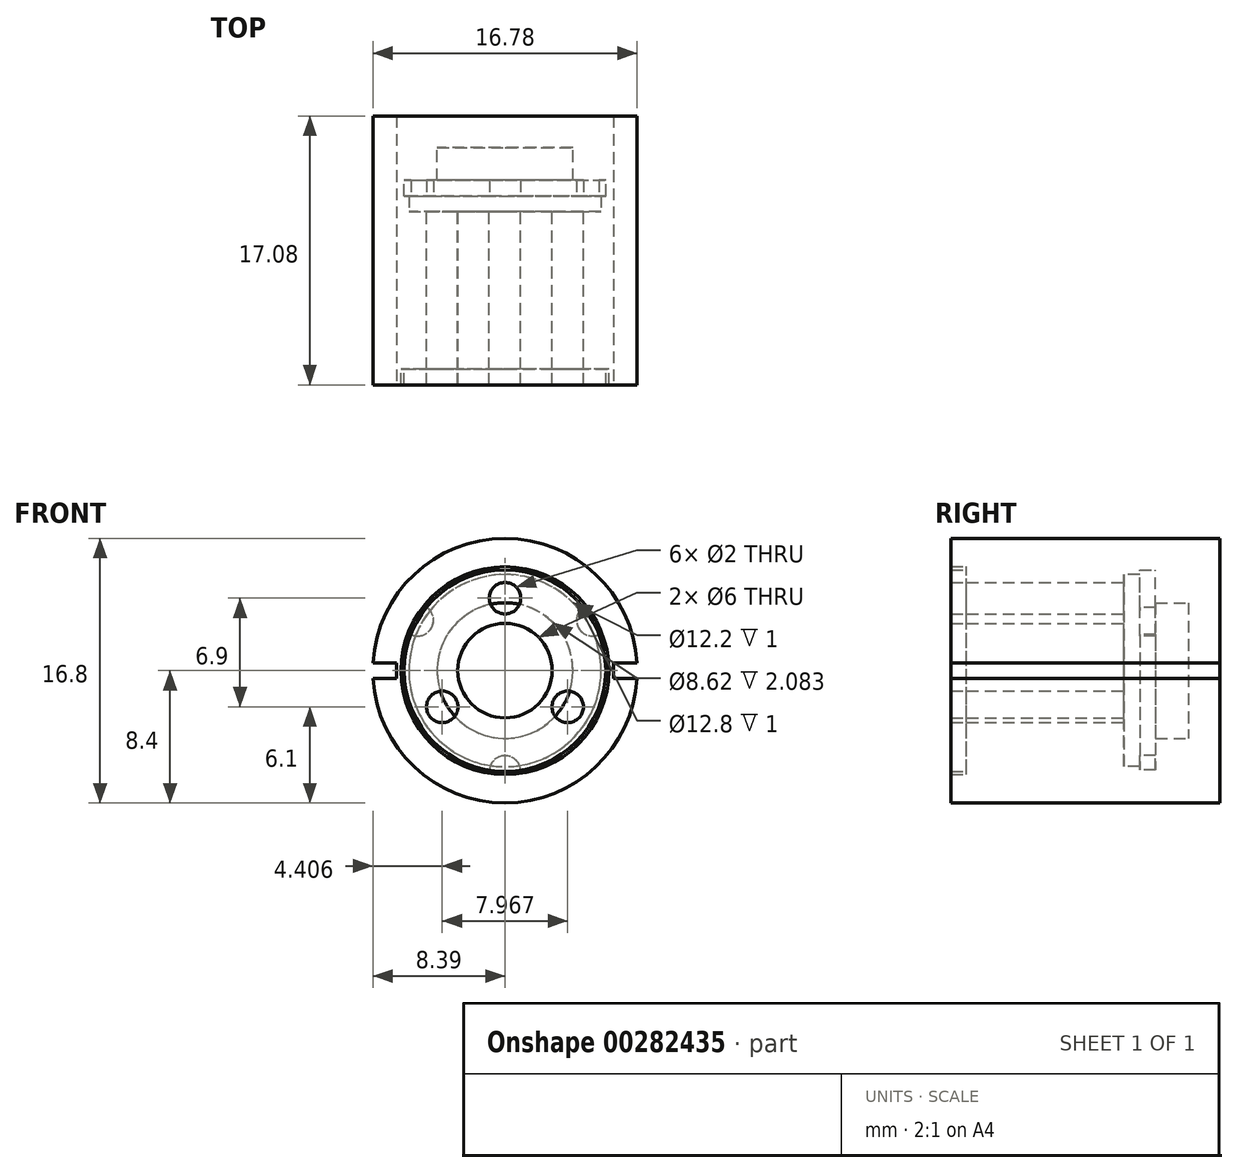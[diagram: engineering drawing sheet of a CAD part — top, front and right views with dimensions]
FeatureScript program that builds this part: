
annotation { "Feature Type Name" : "Feature", "Feature Type Description" : "" }
export const myFeature = defineFeature(function(context is Context, id is Id, definition is map)
    precondition{}
    {
        {
            var Q0;
            Q0=qCreatedBy(makeId("Front.planeOp"),FACE);
            var sketch = newSketch(context, id + "F0", { "sketchPlane" : qUnion([Q0])});
            skCircle(sketch, "E0", {"center": v(0, 0) * mm, "radius": 3 * mm});
            skCircle(sketch, "E1", {"center": v(0, 0) * mm, "radius": 4.6 * mm, "construction": true});
            skCircle(sketch, "E2", {"center": v(0, 0) * mm, "radius": 6.6 * mm});
            skCircle(sketch, "E3", {"center": v(0, 0) * mm, "radius": 10 * mm, "construction": true});
            skCircle(sketch, "E4", {"center": v(0, 4.6) * mm, "radius": 1 * mm});
            skCircle(sketch, "E5.1.0", {"center": v(-3.98, -2.3) * mm, "radius": 1 * mm});
            skCircle(sketch, "E5.2.0", {"center": v(3.98, -2.3) * mm, "radius": 1 * mm});
            skSolve(sketch);
        }
        {
            var Q0;
            Q0 = qSketchRegion(id + "F0", true);
            extrude(context, id + "F1", {"entities" : qUnion([Q0]), "depth" : 10 * mm, "offsetDistance" : 25 * mm});
        }
        {
            var Q0;
            Q0=makeQuery(id+"F1.opExtrude","CAP_FACE",FACE,{"disambiguationData":[OSD([sQuery(id+"F0.wireOp",EDGE,"E0"),sQuery(id+"F0.wireOp",EDGE,"E2"),sQuery(id+"F0.wireOp",EDGE,"E4"),sQuery(id+"F0.wireOp",EDGE,"E5.1.0"),sQuery(id+"F0.wireOp",EDGE,"E5.2.0")])],"isStart":false});
            extrude(context, id + "F2", {"entities" : qUnion([Q0]), "depth" : 1 * mm, "offsetDistance" : 25 * mm});
        }
        {
            var Q0;
            Q0=makeQuery(id+"F1.opExtrude","CAP_FACE",FACE,{"disambiguationData":[OSD([sQuery(id+"F0.wireOp",EDGE,"E0"),sQuery(id+"F0.wireOp",EDGE,"E2"),sQuery(id+"F0.wireOp",EDGE,"E4"),sQuery(id+"F0.wireOp",EDGE,"E5.1.0"),sQuery(id+"F0.wireOp",EDGE,"E5.2.0")])],"isStart":true});
            var sketch = newSketch(context, id + "F3", { "sketchPlane" : qUnion([Q0])});
            skCircle(sketch, "E6", {"center": v(0, 0) * mm, "radius": 6.1 * mm});
            skSolve(sketch);
        }
        {
            var Q0;
            Q0=makeQuery(id+"F3.imprint","IMPRINT",FACE,{"disambiguationData":[TD([[makeQuery(id+"F3.imprint","IMPRINT",EDGE,{"derivedFrom":sQuery(id+"F3.wireOp",EDGE,"E6")}),-1.0]])]});
            extrude(context, id + "F4", {"entities" : qUnion([Q0]), "operationType" : NewBodyOperationType.ADD, "depth" : 1 * mm, "offsetDistance" : 25 * mm});
        }
        {
            var Q0;
            Q0=qCreatedBy(makeId("Top.planeOp"),FACE);
            var sketch = newSketch(context, id + "F5", { "sketchPlane" : qUnion([Q0])});
            skLineSegment(sketch, "E7.0", {"start": v(6.6, 1) * mm, "end": v(-6.6, 1) * mm});
            skLineSegment(sketch, "E8", {"start": v(-6.6, 1) * mm, "end": v(-6.6, 2) * mm});
            skLineSegment(sketch, "E9", {"start": v(-6.6, 2) * mm, "end": v(-4.31, 2) * mm});
            skLineSegment(sketch, "E10.MirrorCS", {"start": v(6.6, 2) * mm, "end": v(4.31, 2) * mm});
            skLineSegment(sketch, "E11.MirrorCS", {"start": v(6.6, 1) * mm, "end": v(6.6, 2) * mm});
            skArc(sketch, "E12", {"start": v(4.31, 2) * mm, "mid": v(0, 4.08) * mm, "end": v(-4.31, 2) * mm, "construction": true});
            skLineSegment(sketch, "E13", {"start": v(0, 4.08) * mm, "end": v(0, 1) * mm});
            skPoint(sketch, "E14", {"position": v(0, 4.08) * mm});
            skLineSegment(sketch, "E15", {"start": v(-4.31, 2) * mm, "end": v(-4.31, 4.08) * mm});
            skLineSegment(sketch, "E16", {"start": v(-4.31, 4.08) * mm, "end": v(4.31, 4.08) * mm});
            skLineSegment(sketch, "E17", {"start": v(4.31, 4.08) * mm, "end": v(4.31, 2) * mm});
            skSolve(sketch);
        }
        {
            var Q0;
            {var subQ3=sQuery(id+"F5.wireOp",EDGE,"E8");Q0=makeQuery(id+"F5.imprint","IMPRINT",FACE,{"disambiguationData":[TD([[makeQuery(id+"F5.imprint","IMPRINT",EDGE,{"derivedFrom":subQ3}),-1.0]])]});}
            var Q1;
            Q1=makeQuery(id+"F1.opExtrude","CAP_EDGE",EDGE,{"disambiguationData":[OSD([sQuery(id+"F0.wireOp",EDGE,"E0")])],"isStart":true});
            revolve(context, id + "F6", {"surfaceOperationType" : NewSurfaceOperationType.NEW, "entities" : qUnion([Q0]), "axis" : qUnion([Q1]), "revolveType" : RevolveType.FULL});
        }
        {
            var Q0;
            Q0=qCreatedBy(makeId("Front.planeOp"),FACE);
            var sketch = newSketch(context, id + "F7", { "sketchPlane" : qUnion([Q0])});
            skCircle(sketch, "E18.0", {"center": v(0, 0) * mm, "radius": 6.6 * mm, "construction": true});
            skCircle(sketch, "E19", {"center": v(0, 0) * mm, "radius": 6.4 * mm});
            skSolve(sketch);
        }
        {
            var Q0;
            Q0=makeQuery(id+"F7.imprint","IMPRINT",FACE,{"disambiguationData":[TD([[makeQuery(id+"F7.imprint","IMPRINT",EDGE,{"derivedFrom":sQuery(id+"F7.wireOp",EDGE,"E19")}),1.0]])]});
            var Q1;
            Q1=sQuery(id+"F7.wireOp",EDGE,"E18.0");
            var Q2;
            Q2=makeQuery(id+"F6.opRevolve","SWEPT_BODY",BODY,{"disambiguationData":[OSD([sQuery(id+"F5.wireOp",EDGE,"E7.0"),sQuery(id+"F5.wireOp",EDGE,"E8"),sQuery(id+"F5.wireOp",EDGE,"E9"),sQuery(id+"F5.wireOp",EDGE,"E12"),sQuery(id+"F5.wireOp",EDGE,"E13")])]});
            var Q3;
            Q3=sQuery(id+"F5.wireOp",VERTEX,"E14");
            var Q4;
            Q4=makeQuery(id+"F4.opExtrude","CAP_FACE",FACE,{"disambiguationData":[OSD([sQuery(id+"F0.wireOp",EDGE,"E2"),sQuery(id+"F3.wireOp",EDGE,"E6")])],"isStart":false});
            extrude(context, id + "F8", {"entities" : qUnion([Q0]), "surfaceEntities" : qUnion([Q1]), "endBound" : BoundingType.UP_TO_VERTEX, "oppositeDirection" : true, "depth" : 25 * mm, "endBoundEntityBody" : qUnion([Q2]), "endBoundEntityVertex" : qUnion([Q3]), "hasOffset" : true, "offsetDistance" : 2 * mm, "offsetOppositeDirection" : true, "hasSecondDirection" : true, "secondDirectionBound" : SecondDirectionBoundingType.UP_TO_SURFACE, "secondDirectionOppositeDirection" : true, "secondDirectionDepth" : 25 * mm, "secondDirectionBoundEntityFace" : qUnion([Q4])});
        }
        {
            var Q0;
            Q0=makeQuery(id+"F8.opExtrude","CAP_FACE",FACE,{"disambiguationData":[OSD([sQuery(id+"F7.wireOp",EDGE,"E19")])],"isStart":true});
            var sketch = newSketch(context, id + "F9", { "sketchPlane" : qUnion([Q0])});
            skCircle(sketch, "E20", {"center": v(0, -6.4) * mm, "radius": 1 * mm});
            skCircle(sketch, "E21.1.0", {"center": v(5.54, 3.2) * mm, "radius": 1 * mm});
            skCircle(sketch, "E21.2.0", {"center": v(-5.54, 3.2) * mm, "radius": 1 * mm});
            skPoint(sketch, "E21.center", {"position": v(0, 0) * mm});
            skSolve(sketch);
        }
        {
            var Q0;
            Q0=makeQuery(id+"F8.opExtrude","CAP_FACE",FACE,{"disambiguationData":[OSD([sQuery(id+"F7.wireOp",EDGE,"E19")])],"isStart":false});
            var sketch = newSketch(context, id + "F10", { "sketchPlane" : qUnion([Q0])});
            skCircle(sketch, "E22", {"center": v(0, 0) * mm, "radius": 8.4 * mm});
            skSolve(sketch);
        }
        {
            var Q0;
            Q0=makeQuery(id+"F6.opRevolve","SWEPT_BODY",BODY,{"disambiguationData":[OSD([sQuery(id+"F5.wireOp",EDGE,"E7.0"),sQuery(id+"F5.wireOp",EDGE,"E8"),sQuery(id+"F5.wireOp",EDGE,"E9"),sQuery(id+"F5.wireOp",EDGE,"E12"),sQuery(id+"F5.wireOp",EDGE,"E13")])]});
            var Q1;
            Q1=makeQuery(id+"F8.opExtrude","SWEPT_BODY",BODY,{"disambiguationData":[OSD([sQuery(id+"F7.wireOp",EDGE,"E19")])]});
            booleanBodies(context, id + "F11", {"operationType" : BooleanOperationType.SUBTRACTION, "tools" : qUnion([Q0]), "targets" : qUnion([Q1])});
        }
        {
            var Q0;
            Q0=makeQuery(id+"F10.imprint","IMPRINT",FACE,{"disambiguationData":[TD([[makeQuery(id+"F10.imprint","IMPRINT",EDGE,{"derivedFrom":sQuery(id+"F10.wireOp",EDGE,"E22")}),1.0]])]});
            var Q1;
            Q1=makeQuery(id+"F2.opExtrude","CAP_FACE",FACE,{"disambiguationData":[OSD([sQuery(id+"F0.wireOp",EDGE,"E0"),sQuery(id+"F0.wireOp",EDGE,"E2"),sQuery(id+"F0.wireOp",EDGE,"E4"),sQuery(id+"F0.wireOp",EDGE,"E5.1.0"),sQuery(id+"F0.wireOp",EDGE,"E5.2.0")])],"isStart":false});
            extrude(context, id + "F12", {"entities" : qUnion([Q0]), "endBound" : BoundingType.UP_TO_SURFACE, "oppositeDirection" : true, "depth" : 25 * mm, "endBoundEntityFace" : qUnion([Q1]), "offsetDistance" : 25 * mm});
        }
        {
            var Q0;
            Q0=makeQuery(id+"F12.opExtrude","CAP_FACE",FACE,{"disambiguationData":[OSD([sQuery(id+"F7.wireOp",EDGE,"E18.0"),sQuery(id+"F10.wireOp",EDGE,"E22")])],"isStart":false});
            var sketch = newSketch(context, id + "F13", { "sketchPlane" : qUnion([Q0])});
            skLineSegment(sketch, "E23.bottom", {"start": v(-8.66, 0.5) * mm, "end": v(-6.9, 0.5) * mm});
            skLineSegment(sketch, "E23.top", {"start": v(-8.66, -0.5) * mm, "end": v(-6.9, -0.5) * mm});
            skLineSegment(sketch, "E23.left", {"start": v(-8.66, 0.5) * mm, "end": v(-8.66, -0.5) * mm});
            skLineSegment(sketch, "E23.right", {"start": v(-6.9, 0.5) * mm, "end": v(-6.9, -0.5) * mm});
            skPoint(sketch, "E23.middle", {"position": v(-7.78, 0) * mm});
            skLineSegment(sketch, "E24.MirrorCS", {"start": v(8.66, 0.5) * mm, "end": v(6.9, 0.5) * mm});
            skLineSegment(sketch, "E25.MirrorCS", {"start": v(8.66, 0.5) * mm, "end": v(8.66, -0.5) * mm});
            skLineSegment(sketch, "E26.MirrorCS", {"start": v(8.66, -0.5) * mm, "end": v(6.9, -0.5) * mm});
            skLineSegment(sketch, "E27.MirrorCS", {"start": v(6.9, 0.5) * mm, "end": v(6.9, -0.5) * mm});
            skSolve(sketch);
        }
        {
            var Q0;
            {var subQ0=sQuery(id+"F13.wireOp",EDGE,"E23.right");Q0=makeQuery(id+"F13.imprint","IMPRINT",FACE,{"disambiguationData":[TD([[makeQuery(id+"F13.imprint","IMPRINT",EDGE,{"derivedFrom":subQ0}),-1.0]])]});}
            var Q1;
            {var subQ0=sQuery(id+"F13.wireOp",EDGE,"E23.left");Q1=makeQuery(id+"F13.imprint","IMPRINT",FACE,{"disambiguationData":[TD([[makeQuery(id+"F13.imprint","IMPRINT",EDGE,{"derivedFrom":subQ0}),1.0]])]});}
            var Q2;
            {var subQ0=sQuery(id+"F13.wireOp",EDGE,"E27.MirrorCS");Q2=makeQuery(id+"F13.imprint","IMPRINT",FACE,{"disambiguationData":[TD([[makeQuery(id+"F13.imprint","IMPRINT",EDGE,{"derivedFrom":subQ0}),1.0]])]});}
            var Q3;
            {var subQ0=sQuery(id+"F13.wireOp",EDGE,"E25.MirrorCS");Q3=makeQuery(id+"F13.imprint","IMPRINT",FACE,{"disambiguationData":[TD([[makeQuery(id+"F13.imprint","IMPRINT",EDGE,{"derivedFrom":subQ0}),-1.0]])]});}
            extrude(context, id + "F14", {"entities" : qUnion([Q0, Q1, Q2, Q3]), "operationType" : NewBodyOperationType.REMOVE, "endBound" : BoundingType.THROUGH_ALL, "oppositeDirection" : true, "depth" : 25 * mm, "offsetDistance" : 25 * mm});
        }
        {
            var Q0;
            {var subQ0=sQuery(id+"F9.wireOp",EDGE,"E21.2.0");var subQ1=makeQuery(id+"F8.opExtrude","CAP_EDGE",EDGE,{"disambiguationData":[OSD([sQuery(id+"F7.wireOp",EDGE,"E19")])],"isStart":true});var subQ2=makeQuery(id+"F9.imprint","INTERSECT",VERTEX,{"disambiguationData":[OD(0.0)],"derivedFrom":[subQ1,subQ0]});Q0=makeQuery(id+"F9.imprint","IMPRINT",FACE,{"disambiguationData":[TD([[makeQuery(id+"F9.imprint","IMPRINT",EDGE,{"disambiguationData":[TD([[subQ2,-1.0]])],"derivedFrom":subQ0}),1.0]])]});}
            var Q1;
            {var subQ0=sQuery(id+"F9.wireOp",EDGE,"E21.1.0");var subQ1=makeQuery(id+"F8.opExtrude","CAP_EDGE",EDGE,{"disambiguationData":[OSD([sQuery(id+"F7.wireOp",EDGE,"E19")])],"isStart":true});var subQ2=makeQuery(id+"F9.imprint","INTERSECT",VERTEX,{"disambiguationData":[OD(0.0)],"derivedFrom":[subQ1,subQ0]});Q1=makeQuery(id+"F9.imprint","IMPRINT",FACE,{"disambiguationData":[TD([[makeQuery(id+"F9.imprint","IMPRINT",EDGE,{"disambiguationData":[TD([[subQ2,-1.0]])],"derivedFrom":subQ0}),1.0]])]});}
            var Q2;
            {var subQ0=sQuery(id+"F9.wireOp",EDGE,"E20");var subQ1=makeQuery(id+"F8.opExtrude","CAP_EDGE",EDGE,{"disambiguationData":[OSD([sQuery(id+"F7.wireOp",EDGE,"E19")])],"isStart":true});var subQ2=makeQuery(id+"F9.imprint","INTERSECT",VERTEX,{"disambiguationData":[OD(0.0)],"derivedFrom":[subQ1,subQ0]});Q2=makeQuery(id+"F9.imprint","IMPRINT",FACE,{"disambiguationData":[TD([[makeQuery(id+"F9.imprint","IMPRINT",EDGE,{"disambiguationData":[TD([[subQ2,1.0]])],"derivedFrom":subQ0}),1.0]])]});}
            var Q3;
            Q3=makeQuery(id+"F8.opExtrude","CAP_FACE",FACE,{"disambiguationData":[OSD([sQuery(id+"F7.wireOp",EDGE,"E19")])],"isStart":false});
            extrude(context, id + "F15", {"entities" : qUnion([Q0, Q1, Q2]), "operationType" : NewBodyOperationType.REMOVE, "endBound" : BoundingType.UP_TO_SURFACE, "oppositeDirection" : true, "depth" : 25 * mm, "endBoundEntityFace" : qUnion([Q3]), "offsetDistance" : 25 * mm});
        }
        {
            var Q0;
            Q0 = qSketchRegion(id + "F9", true);
            var Q1;
            Q1=makeQuery(id+"F12.opExtrude","CAP_FACE",FACE,{"disambiguationData":[OSD([sQuery(id+"F7.wireOp",EDGE,"E19"),sQuery(id+"F10.wireOp",EDGE,"E22")])],"isStart":true});
            var Q2;
            Q2=makeQuery(id+"F4.opExtrude","CAP_FACE",FACE,{"disambiguationData":[OSD([sQuery(id+"F0.wireOp",EDGE,"E2"),sQuery(id+"F3.wireOp",EDGE,"E6")])],"isStart":false});
            extrude(context, id + "F16", {"entities" : qUnion([Q0]), "operationType" : NewBodyOperationType.ADD, "endBound" : BoundingType.UP_TO_SURFACE, "oppositeDirection" : true, "depth" : 25 * mm, "endBoundEntityFace" : qUnion([Q1]), "offsetDistance" : 25 * mm});
        }
    });
